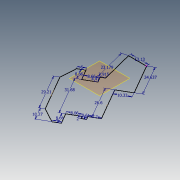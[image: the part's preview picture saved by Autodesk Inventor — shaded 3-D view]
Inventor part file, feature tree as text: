
AUTODESK INVENTOR PART (.ipt)
format: ipt  version: 2014 SP1 (Build 180222100, 222)  size: 112,128 bytes
history: native  units: in
note: dims shown in document units (in); Inventor stores cm internally (conversion verified against a paired STEP export)
features: plane x1, extrude x1
ambient origin geometry x8: Origin, YZ Plane, XZ Plane, XY Plane, X Axis, Y Axis, Z Axis, Center Point
bodies: Solid1 (feature_tree)
feature tree (2):
  plane  "Work Plane3"
  extrude  "Extrusion1"  Depth=1.0472in
